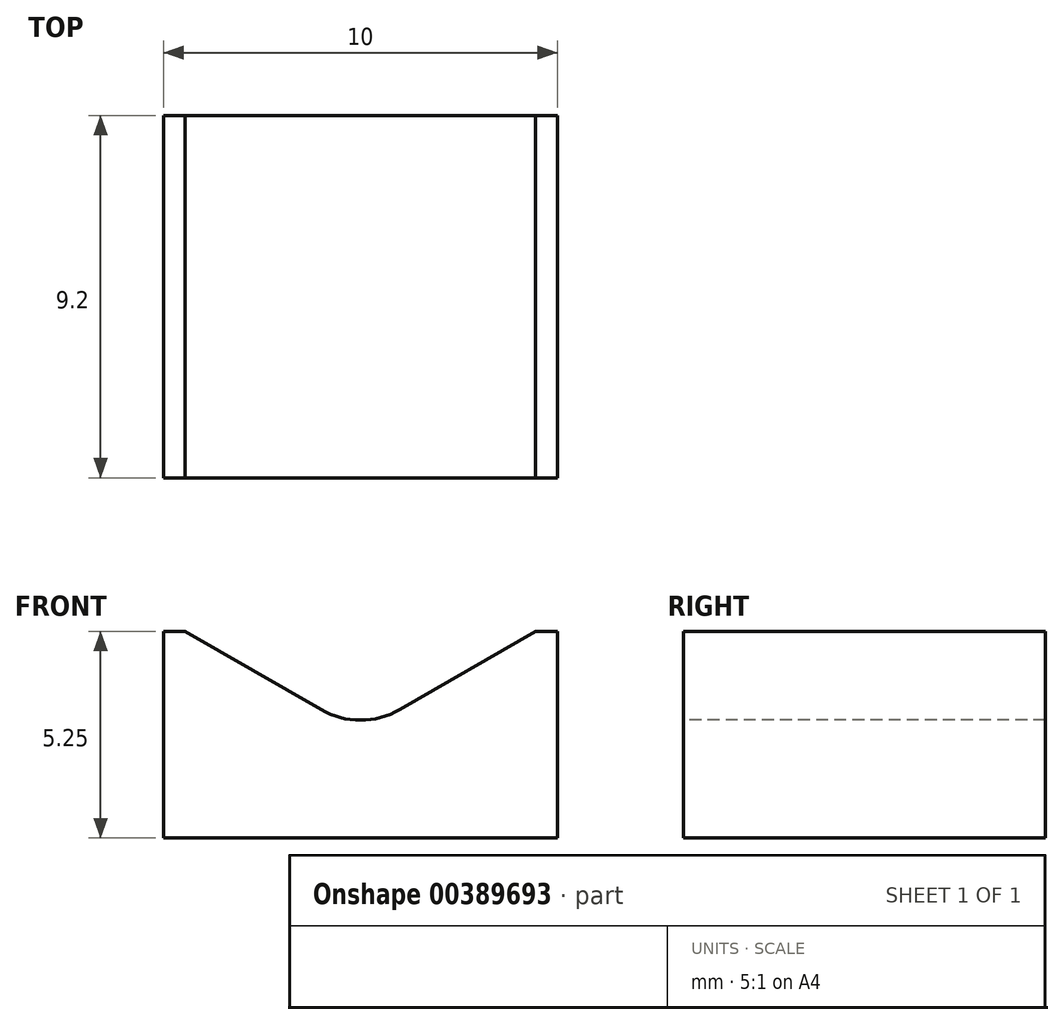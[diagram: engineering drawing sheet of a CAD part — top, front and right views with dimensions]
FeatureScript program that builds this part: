
annotation { "Feature Type Name" : "Feature", "Feature Type Description" : "" }
export const myFeature = defineFeature(function(context is Context, id is Id, definition is map)
    precondition{}
    {
        {
            var Q0;
            Q0=qCreatedBy(makeId("Front.planeOp"),FACE);
            var sketch = newSketch(context, id + "F0", { "sketchPlane" : qUnion([Q0])});
            skLineSegment(sketch, "E0.bottom", {"start": v(0, 0) * mm, "end": v(10, 0) * mm});
            skLineSegment(sketch, "E0.top", {"start": v(0, 5.25) * mm, "end": v(0.55, 5.25) * mm});
            skLineSegment(sketch, "E0.left", {"start": v(0, 0) * mm, "end": v(0, 5.25) * mm});
            skLineSegment(sketch, "E0.right", {"start": v(10, 0) * mm, "end": v(10, 5.25) * mm});
            skPoint(sketch, "E1.endSnap0", {"position": v(5, 5.25) * mm});
            skCircle(sketch, "E2", {"center": v(5, 7.3) * mm, "radius": 4 * mm});
            skLineSegment(sketch, "E3", {"start": v(7, 3.84) * mm, "end": v(9.45, 5.25) * mm});
            skLineSegment(sketch, "E4", {"start": v(9.45, 5.25) * mm, "end": v(5, 2.68) * mm});
            skLineSegment(sketch, "E5", {"start": v(3, 3.84) * mm, "end": v(0.55, 5.25) * mm});
            skLineSegment(sketch, "E6", {"start": v(0.55, 5.25) * mm, "end": v(5, 2.68) * mm});
            skLineSegment(sketch, "E7.trimOffspring", {"start": v(1.57, 5.25) * mm, "end": v(8.43, 5.25) * mm});
            skLineSegment(sketch, "E8.trimOffspring", {"start": v(9.45, 5.25) * mm, "end": v(10, 5.25) * mm});
            skSolve(sketch);
        }
        {
            var Q0;
            Q0=makeQuery(id+"F0.imprint","IMPRINT",FACE,{"disambiguationData":[TD([[makeQuery(id+"F0.imprint","IMPRINT",EDGE,{"derivedFrom":sQuery(id+"F0.wireOp",EDGE,"E0.bottom")}),1.0]])]});
            extrude(context, id + "F1", {"entities" : qUnion([Q0]), "endBound" : BoundingType.SYMMETRIC, "depth" : 9.2 * mm});
        }
        {
            var Q0;
            Q0=makeQuery(id+"F1.opExtrude","SWEPT_EDGE",EDGE,{"disambiguationData":[OSD([sQuery(id+"F0.wireOp",EDGE,"E4"),sQuery(id+"F0.wireOp",EDGE,"E6")])]});
            fillet(context, id + "F2", {"entities" : qUnion([Q0]), "radius" : 2 * mm, "tangentPropagation" : true, "allowEdgeOverflow" : false});
        }
    });
